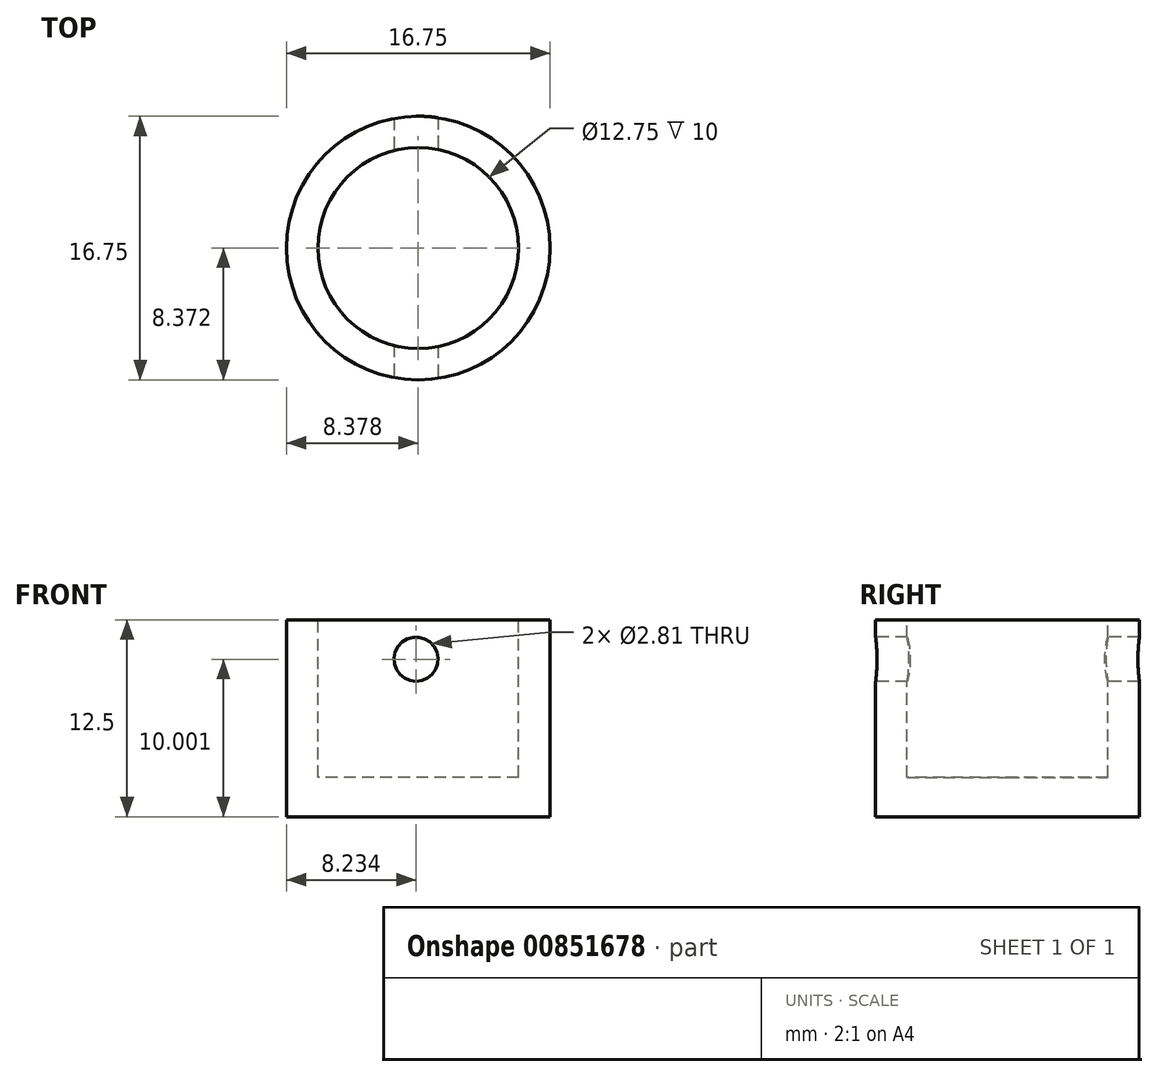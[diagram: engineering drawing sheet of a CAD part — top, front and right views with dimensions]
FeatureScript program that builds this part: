
annotation { "Feature Type Name" : "Feature", "Feature Type Description" : "" }
export const myFeature = defineFeature(function(context is Context, id is Id, definition is map)
    precondition{}
    {
        {
            var Q0;
            Q0=qCreatedBy(makeId("Top.planeOp"),FACE);
            var sketch = newSketch(context, id + "F0", { "sketchPlane" : qUnion([Q0])});
            skCircle(sketch, "E0", {"center": v(19.56, 38.05) * mm, "radius": 8.38 * mm});
            skSolve(sketch);
        }
        {
            var Q0;
            Q0=makeQuery(id+"F0.imprint","IMPRINT",FACE,{"disambiguationData":[TD([[makeQuery(id+"F0.imprint","IMPRINT",EDGE,{"derivedFrom":sQuery(id+"F0.wireOp",EDGE,"E0")}),1.0]])]});
            extrude(context, id + "F1", {"entities" : qUnion([Q0]), "depth" : 12.5 * mm, "offsetDistance" : 25 * mm});
        }
        {
            var Q0;
            Q0=makeQuery(id+"F1.opExtrude","CAP_FACE",FACE,{"disambiguationData":[OSD([sQuery(id+"F0.wireOp",EDGE,"E0")])],"isStart":false});
            var sketch = newSketch(context, id + "F2", { "sketchPlane" : qUnion([Q0])});
            skCircle(sketch, "E1.0", {"center": v(19.56, 38.05) * mm, "radius": 6.38 * mm});
            skSolve(sketch);
        }
        {
            var Q0;
            Q0=makeQuery(id+"F2.imprint","IMPRINT",FACE,{"disambiguationData":[TD([[makeQuery(id+"F2.imprint","IMPRINT",EDGE,{"derivedFrom":sQuery(id+"F2.wireOp",EDGE,"E1.0")}),1.0]])]});
            extrude(context, id + "F3", {"entities" : qUnion([Q0]), "operationType" : NewBodyOperationType.REMOVE, "oppositeDirection" : true, "depth" : 10 * mm, "offsetDistance" : 25 * mm});
        }
        {
            var Q0;
            Q0=qCreatedBy(makeId("Front.planeOp"),FACE);
            var sketch = newSketch(context, id + "F4", { "sketchPlane" : qUnion([Q0])});
            skCircle(sketch, "E2", {"center": v(19.41, 10) * mm, "radius": 1.4 * mm});
            skSolve(sketch);
        }
        {
            var Q0;
            Q0=makeQuery(id+"F4.imprint","IMPRINT",FACE,{"disambiguationData":[TD([[makeQuery(id+"F4.imprint","IMPRINT",EDGE,{"derivedFrom":sQuery(id+"F4.wireOp",EDGE,"E2")}),1.0]])]});
            extrude(context, id + "F5", {"entities" : qUnion([Q0]), "operationType" : NewBodyOperationType.REMOVE, "oppositeDirection" : true, "depth" : 75 * mm, "offsetDistance" : 25 * mm});
        }
    });
